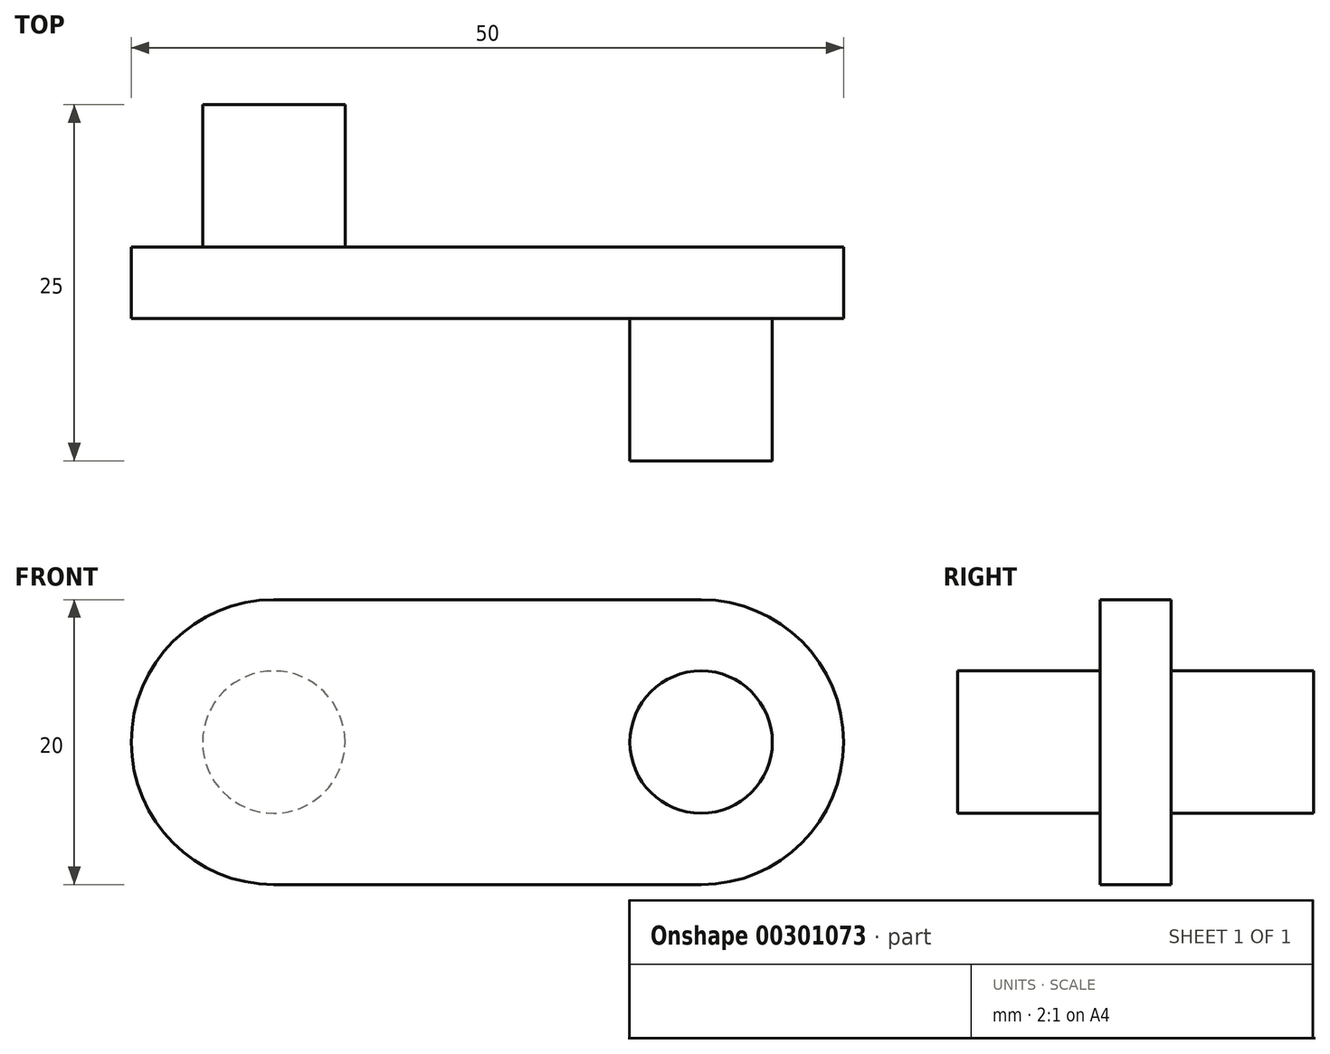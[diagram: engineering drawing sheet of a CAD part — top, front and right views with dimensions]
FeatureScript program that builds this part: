
annotation { "Feature Type Name" : "Feature", "Feature Type Description" : "" }
export const myFeature = defineFeature(function(context is Context, id is Id, definition is map)
    precondition{}
    {
        {
            var Q0;
            Q0=qCreatedBy(makeId("Front.planeOp"),FACE);
            var sketch = newSketch(context, id + "F0", { "sketchPlane" : qUnion([Q0])});
            skLineSegment(sketch, "E0", {"start": v(0, 0) * mm, "end": v(30, 0) * mm});
            skLineSegment(sketch, "E1", {"start": v(30, 20) * mm, "end": v(0, 20) * mm});
            skArc(sketch, "E2", {"start": v(30, 20) * mm, "mid": v(40, 10) * mm, "end": v(30, 0) * mm});
            skArc(sketch, "E3", {"start": v(0, 20) * mm, "mid": v(-10, 10) * mm, "end": v(0, 0) * mm});
            skSolve(sketch);
        }
        {
            var Q0;
            Q0=makeQuery(id+"F0.imprint","IMPRINT",FACE,{"disambiguationData":[TD([[makeQuery(id+"F0.imprint","IMPRINT",EDGE,{"derivedFrom":sQuery(id+"F0.wireOp",EDGE,"E0")}),1.0]])]});
            extrude(context, id + "F1", {"entities" : qUnion([Q0]), "depth" : 5 * mm});
        }
        {
            var Q0;
            Q0=makeQuery(id+"F1.opExtrude","CAP_FACE",FACE,{"disambiguationData":[OSD([sQuery(id+"F0.wireOp",EDGE,"E0"),sQuery(id+"F0.wireOp",EDGE,"E1"),sQuery(id+"F0.wireOp",EDGE,"E2"),sQuery(id+"F0.wireOp",EDGE,"E3")])],"isStart":false});
            var sketch = newSketch(context, id + "F2", { "sketchPlane" : qUnion([Q0])});
            skCircle(sketch, "E4", {"center": v(30, 10) * mm, "radius": 5 * mm});
            skSolve(sketch);
        }
        {
            var Q0;
            Q0 = qSketchRegion(id + "F2", true);
            extrude(context, id + "F3", {"entities" : qUnion([Q0]), "operationType" : NewBodyOperationType.ADD, "depth" : 10 * mm});
        }
        {
            var Q0;
            Q0=makeQuery(id+"F0.imprint","IMPRINT",FACE,{"disambiguationData":[TD([[makeQuery(id+"F0.imprint","IMPRINT",EDGE,{"derivedFrom":sQuery(id+"F0.wireOp",EDGE,"E0")}),1.0]])]});
            var sketch = newSketch(context, id + "F4", { "sketchPlane" : qUnion([Q0])});
            skCircle(sketch, "E5", {"center": v(0, 10) * mm, "radius": 5 * mm});
            skSolve(sketch);
        }
        {
            var Q0;
            Q0 = qSketchRegion(id + "F4", true);
            extrude(context, id + "F5", {"entities" : qUnion([Q0]), "operationType" : NewBodyOperationType.ADD, "oppositeDirection" : true, "depth" : 10 * mm});
        }
    });
